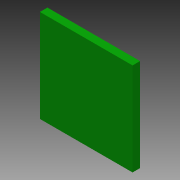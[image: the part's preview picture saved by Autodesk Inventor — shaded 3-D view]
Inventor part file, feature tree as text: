
AUTODESK INVENTOR PART (.ipt)
format: ipt  version: 2014 (Build 180170000, 170)  size: 71,680 bytes
history: native  units: in
note: dims shown in document units (in); Inventor stores cm internally (conversion verified against a paired STEP export)
features: extrude x1, sketch x1
ambient origin geometry x8: Origin, YZ Plane, XZ Plane, XY Plane, X Axis, Y Axis, Z Axis, Center Point
bodies: Solid1 (feature_tree)
feature tree (2):
  extrude  "Extrusion1"  Depth=0.29in
  sketch  "Sketch1"  dims[d0=0.29in d1=0.29in d2=0.0236in d3=0.0in d4=0.145in d5=0.145in]
